# Revit family: 6NDMLH-NRG
name_source: partatom
category: Mechanical Equipment
units: mm (PartAtom-declared; Revit-internal decimal feet)

## family parameters
Always vertical = Yes
Cut with Voids When Loaded = No
OmniClass Number = 23.40.40.11.17
OmniClass Title = Refrigerated Cases
Part Type = Normal
Room Calculation Point = No
Round Connector Dimension = Use Radius
Shared = No
Work Plane-Based = Yes

## types (4) — shared parameters
20" Shelf = Yes
BOTTOM ELECTRICAL = Yes
BOTTOM REFRIGERATION PIPING = Yes
Certifications = NSF 7, UL471, CSA
DATE = 03/13/2017
DRAIN PIPING = Yes
Default Elevation = 48"
Description = Narrow Multi-Deck Merchandiser with Synerg-E™
Discharge Air Velocity (FPM) = 260 FPM
EQUIPMENT DESCRIPTION = Narrow Multi-Deck Merchandiser with Synerg-E™
EQUIPMENT MARK = 6NDMLH-NRG
FULL VIEW LH END = Yes
FULL VIEW RH END = Yes
GLASS = Glass
Height = 88 5/8"
Item Description = Narrow Multi-Deck Merchandiser with Synerg-E™
LF STD END = Yes
Legend Number = 6NDMLH-NRG
Manufacturer = HILL PHOENIX
Model = 6NDMLH-NRG
PAINTED METAL UPPER SHELF = PAINTED SHELVES
REAR REFRIGERATION PIPING = Yes
REDUCED VIEW LH END = Yes
REDUCED VIEW RH END = Yes
REFRIGERATION PIPING = COPPER PIPE
RT STD END = Yes
SOLID EXT LH END = Yes
SOLID EXT RH END = Yes
SOLID STD LH END = Yes
SOLID STD RH END = Yes
SQUARE LH END = Yes
SQUARE RH END = Yes
STAINLESS STEEL = GALVANIZED STEEL
SUPER VIEW LH END = Yes
SUPER VIEW RH END = Yes
Standard Power Amps = 0 A
Superheat Set Point @ Bulb (°F) = 6-8 °F
TOP ELECTRICAL = Yes
TOP REFRIGERATION PIPING = Yes
Timed-Off Defrost Termination Temp = 42 °F
URL = http://www.hillphoenix.com
Width = 37 3/4"

## per-type parameters (varying)
| type | BTUH Conventional | BTUH Parallel | CENTER LINE | DRAIN LINE | Defrosts Per Day | Discharge Air (°F) | Evaporator (°F) | High Efficiency Amps | High Efficiency Watts | High Power (Cornice) Amps | High Power (Cornice) Watts | Length | Length of Cases | Light Length | Lights Per Row | Number of Fans | Refgn | Standard Power Watts | Timed-Off Defrost Fail-Safe (Min) |
| 04' | 1862 | 1748 | 24" | 36" | 6 | 31 °F | 28 °F | 0 A | 43 W | 0 A | 15 W | 48" | 48" | 4' | 1 | 2 | 7 5/8" | 6 W | 45 |
| 08' | 1862 | 1748 | 48" | 48" | 6 | 31 °F | 28 °F | 1 A | 65 W | 0 A | 30 W | 96" | 96" | 4' | 2 | 3 | 8 3/4" | 12 W | 45 (Min) |
| 12' | 1862 | 1748 | 72" | 72" | 6 | 31 °F | 28 °F | 1 A | 87 W | 1 A | 65 W | 144" | 144" | 4' | 3 | 4 | 8 3/4" | 36 W | 45 (Min) |
| 06' | 1860 | 1819 | 36" | 48" | 2 | 37 °F | 34 °F | 1 A | 65 W | 0 A | 24 W | 72" | 72" | 3' | 2 | 3 | 8 3/4" | 9 W | 30 |

## geometry (parser evidence)
native form markers: Blend x19, Sweep x10
no freeform markers — native parametric forms only
